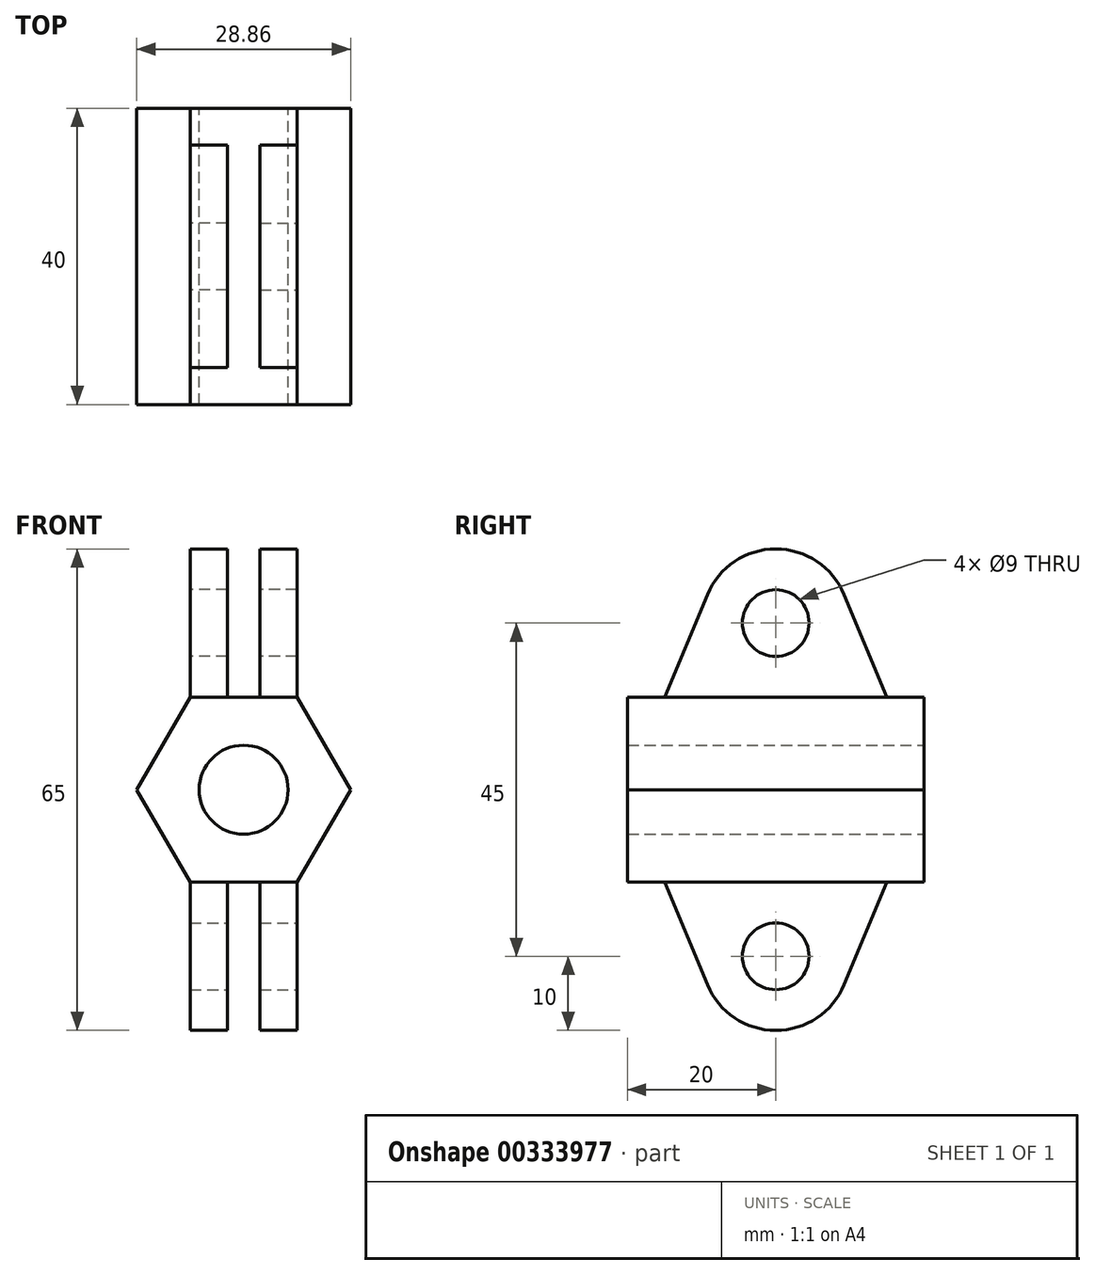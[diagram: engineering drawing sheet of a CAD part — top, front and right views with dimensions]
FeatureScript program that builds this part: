
annotation { "Feature Type Name" : "Feature", "Feature Type Description" : "" }
export const myFeature = defineFeature(function(context is Context, id is Id, definition is map)
    precondition{}
    {
        {
            var Q0;
            Q0=qCreatedBy(makeId("Front.planeOp"),FACE);
            var sketch = newSketch(context, id + "F0", { "sketchPlane" : qUnion([Q0])});
            skCircle(sketch, "E0", {"center": v(0, 0) * mm, "radius": 6 * mm});
            skCircle(sketch, "E1.cCircle", {"center": v(0, 0) * mm, "radius": 12.5 * mm, "construction": true});
            skLineSegment(sketch, "E1.0", {"start": v(-7.22, 12.5) * mm, "end": v(7.22, 12.5) * mm});
            skLineSegment(sketch, "E1.1", {"start": v(7.22, 12.5) * mm, "end": v(14.43, 0) * mm});
            skLineSegment(sketch, "E1.2", {"start": v(14.43, 0) * mm, "end": v(7.22, -12.5) * mm});
            skLineSegment(sketch, "E1.3", {"start": v(7.22, -12.5) * mm, "end": v(-7.22, -12.5) * mm});
            skLineSegment(sketch, "E1.4", {"start": v(-7.22, -12.5) * mm, "end": v(-14.43, 0) * mm});
            skLineSegment(sketch, "E1.5", {"start": v(-14.43, 0) * mm, "end": v(-7.22, 12.5) * mm});
            skPoint(sketch, "E1.0.midPoint", {"position": v(0, 12.5) * mm});
            skSolve(sketch);
        }
        {
            var Q0;
            Q0 = qSketchRegion(id + "F0", true);
            extrude(context, id + "F1", {"entities" : qUnion([Q0]), "endBound" : BoundingType.SYMMETRIC, "depth" : 40 * mm});
        }
        {
            var Q0;
            Q0=makeQuery(id+"F1.opExtrude","SWEPT_FACE",FACE,{"disambiguationData":[OSD([sQuery(id+"F0.wireOp",EDGE,"E1.0")])]});
            var sketch = newSketch(context, id + "F2", { "sketchPlane" : qUnion([Q0])});
            skLineSegment(sketch, "E2.bottom", {"start": v(7.22, 15) * mm, "end": v(-7.22, 15) * mm});
            skLineSegment(sketch, "E2.top", {"start": v(7.22, -15) * mm, "end": v(-7.22, -15) * mm});
            skLineSegment(sketch, "E2.left", {"start": v(7.22, 15) * mm, "end": v(7.22, -15) * mm});
            skLineSegment(sketch, "E2.right", {"start": v(-7.22, 15) * mm, "end": v(-7.22, -15) * mm});
            skSolve(sketch);
        }
        {
            var Q0;
            Q0 = qSketchRegion(id + "F2", true);
            extrude(context, id + "F3", {"entities" : qUnion([Q0]), "operationType" : NewBodyOperationType.ADD, "depth" : 20 * mm});
        }
        {
            var Q0;
            Q0=makeQuery(id+"F3.opExtrude","SWEPT_FACE",FACE,{"disambiguationData":[OSD([sQuery(id+"F2.wireOp",EDGE,"E2.right")])]});
            var sketch = newSketch(context, id + "F4", { "sketchPlane" : qUnion([Q0])});
            skCircle(sketch, "E3", {"center": v(0, 22.5) * mm, "radius": 4.5 * mm});
            skSolve(sketch);
        }
        {
            var Q0;
            Q0=makeQuery(id+"F4.imprint","IMPRINT",FACE,{"disambiguationData":[TD([[makeQuery(id+"F4.imprint","IMPRINT",EDGE,{"derivedFrom":sQuery(id+"F4.wireOp",EDGE,"E3")}),1.0]])]});
            extrude(context, id + "F5", {"entities" : qUnion([Q0]), "operationType" : NewBodyOperationType.REMOVE, "endBound" : BoundingType.THROUGH_ALL, "oppositeDirection" : true, "depth" : 100 * mm});
        }
        {
            var Q0;
            Q0=makeQuery(id+"F3.opExtrude","SWEPT_FACE",FACE,{"disambiguationData":[OSD([sQuery(id+"F2.wireOp",EDGE,"E2.right")])]});
            var sketch = newSketch(context, id + "F6", { "sketchPlane" : qUnion([Q0])});
            skLineSegment(sketch, "E4", {"start": v(0, 12.5) * mm, "end": v(-15, 12.5) * mm});
            skLineSegment(sketch, "E5", {"start": v(-15, 12.5) * mm, "end": v(-9.23, 26.35) * mm});
            skLineSegment(sketch, "E6.MirrorCS", {"start": v(15, 12.5) * mm, "end": v(9.23, 26.35) * mm});
            skLineSegment(sketch, "E7.MirrorCS", {"start": v(0, 12.5) * mm, "end": v(15, 12.5) * mm});
            skArc(sketch, "E8", {"start": v(9.23, 26.35) * mm, "mid": v(0, 32.5) * mm, "end": v(-9.23, 26.35) * mm});
            skSolve(sketch);
        }
        {
            var Q0;
            {var subQ0=sQuery(id+"F6.wireOp",EDGE,"E5");Q0=makeQuery(id+"F6.imprint","IMPRINT",FACE,{"disambiguationData":[TD([[makeQuery(id+"F6.imprint","IMPRINT",EDGE,{"derivedFrom":subQ0}),1.0]])]});}
            var Q1;
            {var subQ0=sQuery(id+"F6.wireOp",EDGE,"E6.MirrorCS");Q1=makeQuery(id+"F6.imprint","IMPRINT",FACE,{"disambiguationData":[TD([[makeQuery(id+"F6.imprint","IMPRINT",EDGE,{"derivedFrom":subQ0}),-1.0]])]});}
            extrude(context, id + "F7", {"entities" : qUnion([Q0, Q1]), "operationType" : NewBodyOperationType.REMOVE, "oppositeDirection" : true, "depth" : 25.4 * mm});
        }
        {
            var Q0;
            {var subQ2=sQuery(id+"F0.wireOp",EDGE,"E1.0");Q0=makeQuery(id+"F3.boolean.opBoolean","SPLIT",FACE,{"disambiguationData":[TD([makeQuery(id+"F3.opExtrude","SWEPT_FACE",FACE,{"disambiguationData":[OSD([sQuery(id+"F2.wireOp",EDGE,"E2.bottom")])]})])],"derivedFrom":makeQuery(id+"F1.opExtrude","SWEPT_FACE",FACE,{"disambiguationData":[OSD([subQ2])]})});}
            var sketch = newSketch(context, id + "F8", { "sketchPlane" : qUnion([Q0])});
            skLineSegment(sketch, "E9.bottom", {"start": v(-2.22, 20) * mm, "end": v(2.22, 20) * mm});
            skLineSegment(sketch, "E9.top", {"start": v(-2.22, -20) * mm, "end": v(2.22, -20) * mm});
            skLineSegment(sketch, "E9.left", {"start": v(-2.22, 20) * mm, "end": v(-2.22, -20) * mm});
            skLineSegment(sketch, "E9.right", {"start": v(2.22, 20) * mm, "end": v(2.22, -20) * mm});
            skSolve(sketch);
        }
        {
            var Q0;
            Q0 = qSketchRegion(id + "F8", true);
            extrude(context, id + "F9", {"entities" : qUnion([Q0]), "operationType" : NewBodyOperationType.REMOVE, "depth" : 25.4 * mm});
        }
        {
            var Q0;
            Q0=makeQuery(id+"F1.opExtrude","SWEPT_FACE",FACE,{"disambiguationData":[OSD([sQuery(id+"F0.wireOp",EDGE,"E1.3")])]});
            var sketch = newSketch(context, id + "F10", { "sketchPlane" : qUnion([Q0])});
            skLineSegment(sketch, "E10.bottom", {"start": v(-7.22, -15) * mm, "end": v(7.22, -15) * mm});
            skLineSegment(sketch, "E10.top", {"start": v(-7.22, 15) * mm, "end": v(7.22, 15) * mm});
            skLineSegment(sketch, "E10.left", {"start": v(-7.22, -15) * mm, "end": v(-7.22, 15) * mm});
            skLineSegment(sketch, "E10.right", {"start": v(7.22, -15) * mm, "end": v(7.22, 15) * mm});
            skSolve(sketch);
        }
        {
            var Q0;
            Q0 = qSketchRegion(id + "F10", true);
            extrude(context, id + "F11", {"entities" : qUnion([Q0]), "operationType" : NewBodyOperationType.ADD, "depth" : 20 * mm});
        }
        {
            var Q0;
            Q0=makeQuery(id+"F11.opExtrude","SWEPT_FACE",FACE,{"disambiguationData":[OSD([sQuery(id+"F10.wireOp",EDGE,"E10.right")])]});
            var sketch = newSketch(context, id + "F12", { "sketchPlane" : qUnion([Q0])});
            skCircle(sketch, "E11", {"center": v(0, -22.5) * mm, "radius": 4.5 * mm});
            skPoint(sketch, "E11.centerSnap0", {"position": v(0, -12.5) * mm});
            skSolve(sketch);
        }
        {
            var Q0;
            Q0 = qSketchRegion(id + "F12", true);
            extrude(context, id + "F13", {"entities" : qUnion([Q0]), "operationType" : NewBodyOperationType.REMOVE, "oppositeDirection" : true, "depth" : 25.4 * mm});
        }
        {
            var Q0;
            Q0=makeQuery(id+"F11.opExtrude","SWEPT_FACE",FACE,{"disambiguationData":[OSD([sQuery(id+"F10.wireOp",EDGE,"E10.right")])]});
            var sketch = newSketch(context, id + "F14", { "sketchPlane" : qUnion([Q0])});
            skLineSegment(sketch, "E12", {"start": v(0, -12.5) * mm, "end": v(15, -12.5) * mm});
            skLineSegment(sketch, "E13", {"start": v(15, -12.5) * mm, "end": v(9.23, -26.35) * mm});
            skLineSegment(sketch, "E14.MirrorCS", {"start": v(-15, -12.5) * mm, "end": v(-9.23, -26.35) * mm});
            skLineSegment(sketch, "E15.MirrorCS", {"start": v(0, -12.5) * mm, "end": v(-15, -12.5) * mm});
            skArc(sketch, "E16", {"start": v(-9.23, -26.35) * mm, "mid": v(0, -32.5) * mm, "end": v(9.23, -26.35) * mm});
            skSolve(sketch);
        }
        {
            var Q0;
            {var subQ0=sQuery(id+"F14.wireOp",EDGE,"E13");Q0=makeQuery(id+"F14.imprint","IMPRINT",FACE,{"disambiguationData":[TD([[makeQuery(id+"F14.imprint","IMPRINT",EDGE,{"derivedFrom":subQ0}),1.0]])]});}
            var Q1;
            {var subQ0=sQuery(id+"F14.wireOp",EDGE,"E14.MirrorCS");Q1=makeQuery(id+"F14.imprint","IMPRINT",FACE,{"disambiguationData":[TD([[makeQuery(id+"F14.imprint","IMPRINT",EDGE,{"derivedFrom":subQ0}),-1.0]])]});}
            extrude(context, id + "F15", {"entities" : qUnion([Q0, Q1]), "operationType" : NewBodyOperationType.REMOVE, "oppositeDirection" : true, "depth" : 25.4 * mm});
        }
        {
            var Q0;
            {var subQ2=sQuery(id+"F0.wireOp",EDGE,"E1.3");Q0=makeQuery(id+"F11.boolean.opBoolean","SPLIT",FACE,{"disambiguationData":[TD([makeQuery(id+"F11.opExtrude","SWEPT_FACE",FACE,{"disambiguationData":[OSD([sQuery(id+"F10.wireOp",EDGE,"E10.bottom")])]})])],"derivedFrom":makeQuery(id+"F1.opExtrude","SWEPT_FACE",FACE,{"disambiguationData":[OSD([subQ2])]})});}
            var sketch = newSketch(context, id + "F16", { "sketchPlane" : qUnion([Q0])});
            skLineSegment(sketch, "E17.bottom", {"start": v(-2.22, -20) * mm, "end": v(2.22, -20) * mm});
            skLineSegment(sketch, "E17.top", {"start": v(-2.22, 20) * mm, "end": v(2.22, 20) * mm});
            skLineSegment(sketch, "E17.left", {"start": v(-2.22, -20) * mm, "end": v(-2.22, 20) * mm});
            skLineSegment(sketch, "E17.right", {"start": v(2.22, -20) * mm, "end": v(2.22, 20) * mm});
            skSolve(sketch);
        }
        {
            var Q0;
            Q0 = qSketchRegion(id + "F16", true);
            extrude(context, id + "F17", {"entities" : qUnion([Q0]), "operationType" : NewBodyOperationType.REMOVE, "depth" : 25.4 * mm});
        }
    });
